# Revit family: Skope BB580
name_source: partatom
category: Specialty Equipment
revit_build: Autodesk Revit 2015 (Build: 20140606_1530(x64)
units: mm (PartAtom-declared; Revit-internal decimal feet)

## types (8) — shared parameters
Bench Thickness = 40 mm  [stored 0.131234 ft]
Door Thickness = 71 mm
Door Width = 560 mm  [stored 1.83727 ft]
DoorNo = 3
Interior Wheel Offset = 90 mm  [stored 0.295276 ft]
Large Unit Size = 380 mm
MH = 880 mm  [stored 2.88714 ft]
MS = 1680 mm  [stored 5.51181 ft]
MW = 525 mm
Manufacturer = Skope Ltd.
Overall Depth = 920 mm  [stored 3.01837 ft]
Overall Width = 596 mm  [stored 1.95538 ft]
Small Unit Size = 235 mm  [stored 0.770997 ft]

## per-type parameters (varying)
| type | LH Refrigeration Unit | LH Unit | LHL | LHS | Large Refrigeration Unit | Model | Overall Length | RH Refrigeration Unit | RH Unit | RHL | RHS | Refridgeration Unit Depth | Sliding | Small Refrigeration Unit | Swing |
| 3 Sliding Doors Chiller Integral (LH) | 380 mm | Yes | Yes | No | Yes | BB580-3SL | 2060 mm  [stored 6.75853 ft] | 0 mm  [stored 0 ft] | No | No | No | 380 mm | Yes | No | No |
| 3 Sliding Doors Chiller Integral (RH) | 0 mm  [stored 0 ft] | No | No | No | Yes | BB580-3SL-RH | 2060 mm  [stored 6.75853 ft] | 380 mm | Yes | Yes | No | 380 mm | Yes | No | No |
| 3 Sliding Doors Chiller Remote (LH) | 235 mm  [stored 0.770997 ft] | Yes | No | Yes | No | BB580r-3SL | 1915 mm  [stored 6.28281 ft] | 0 mm  [stored 0 ft] | No | No | No | 235 mm  [stored 0.770997 ft] | Yes | Yes | No |
| 3 Sliding Doors Chiller Remote (RH) | 0 mm  [stored 0 ft] | No | No | No | No | BB580r-3SL-RH | 1915 mm  [stored 6.28281 ft] | 235 mm  [stored 0.770997 ft] | Yes | No | Yes | 235 mm  [stored 0.770997 ft] | Yes | Yes | No |
| 3 Swing Doors Chiller Integral (LH) | 380 mm | Yes | Yes | No | Yes | BB580-3SW | 2060 mm  [stored 6.75853 ft] | 0 mm  [stored 0 ft] | No | No | No | 380 mm | No | No | Yes |
| 3 Swing Doors Chiller Integral (RH) | 0 mm  [stored 0 ft] | No | No | No | Yes | BB580-3SW-RH | 2060 mm  [stored 6.75853 ft] | 380 mm | Yes | Yes | No | 380 mm | No | No | Yes |
| 3 Swing Doors Chiller Remote (LH) | 235 mm  [stored 0.770997 ft] | Yes | No | Yes | No | BB580r-3SW | 1915 mm  [stored 6.28281 ft] | 0 mm  [stored 0 ft] | No | No | No | 235 mm  [stored 0.770997 ft] | No | Yes | Yes |
| 3 Swing Doors Chiller Remote (RH) | 0 mm  [stored 0 ft] | No | No | No | No | BB580r-3SW-RH | 1915 mm  [stored 6.28281 ft] | 235 mm  [stored 0.770997 ft] | Yes | No | Yes | 235 mm  [stored 0.770997 ft] | No | Yes | Yes |

note: column(s) folded — value = type name in every type: Description

note: [stored X ft] marks values corroborated as IEEE doubles in the binary element streams (Revit-internal decimal feet)

## geometry (parser evidence)
native form markers: Sweep x55
no freeform markers — native parametric forms only
